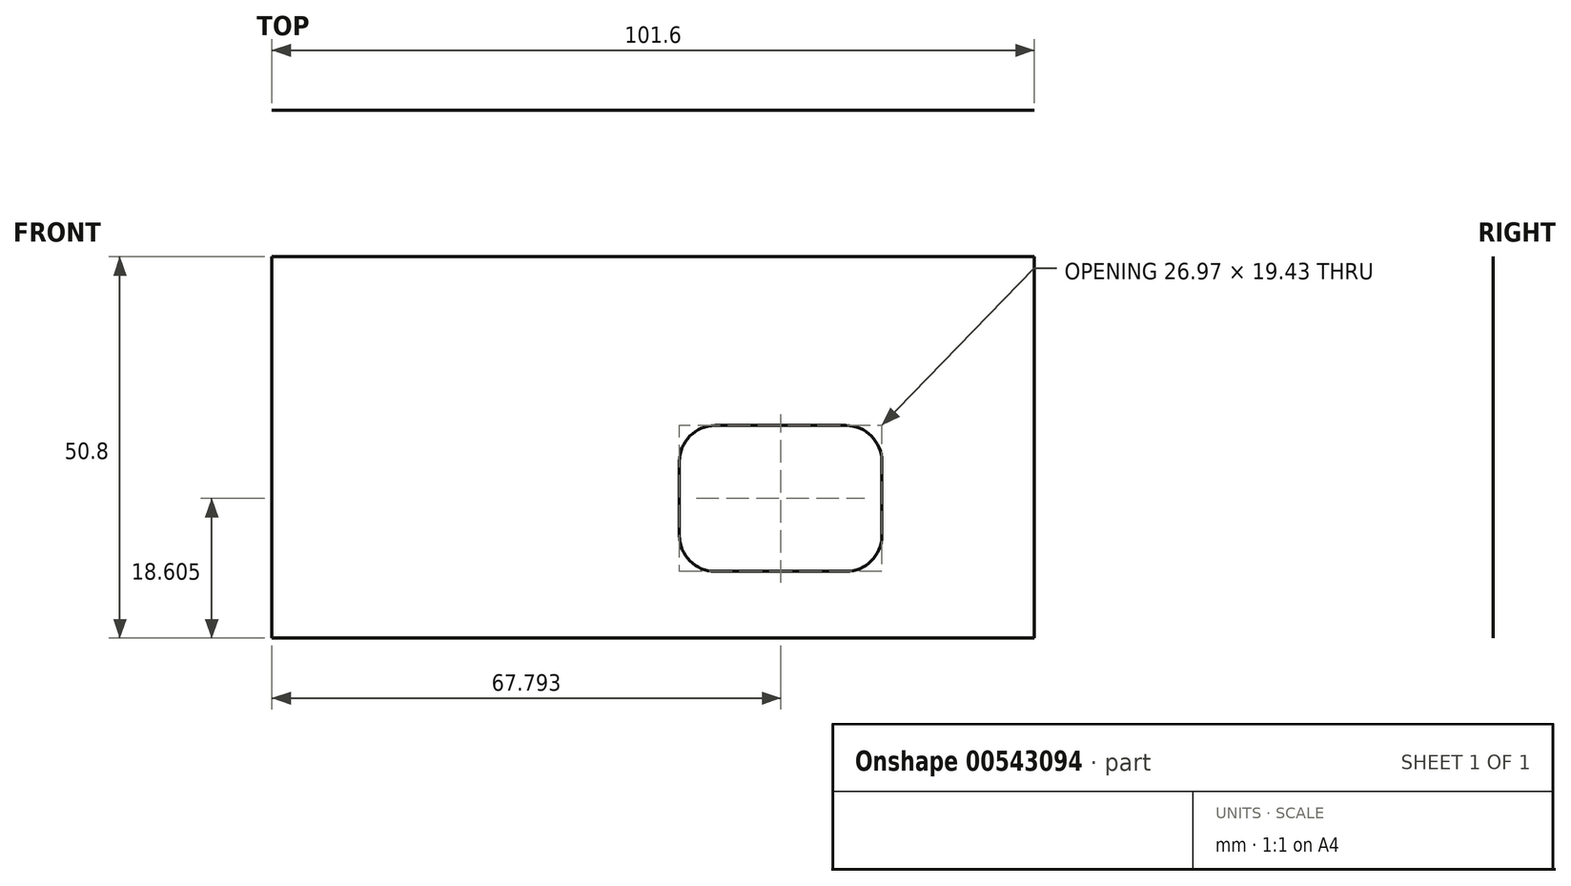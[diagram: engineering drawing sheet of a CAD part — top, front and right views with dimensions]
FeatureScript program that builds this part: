
annotation { "Feature Type Name" : "Feature", "Feature Type Description" : "" }
export const myFeature = defineFeature(function(context is Context, id is Id, definition is map)
    precondition{}
    {
        {
            var Q0;
            Q0=qCreatedBy(makeId("Front.planeOp"),FACE);
            var sketch = newSketch(context, id + "F0", { "sketchPlane" : qUnion([Q0])});
            skLineSegment(sketch, "E0.bottom", {"start": v(0, 0) * mm, "end": v(101.6, 0) * mm});
            skLineSegment(sketch, "E0.top", {"start": v(0, 50.8) * mm, "end": v(101.6, 50.8) * mm});
            skLineSegment(sketch, "E0.left", {"start": v(0, 0) * mm, "end": v(0, 50.8) * mm});
            skLineSegment(sketch, "E0.right", {"start": v(101.6, 0) * mm, "end": v(101.6, 50.8) * mm});
            skLineSegment(sketch, "E1.bottom", {"start": v(76.52, 8.9) * mm, "end": v(59.07, 8.89) * mm});
            skLineSegment(sketch, "E1.top", {"start": v(76.52, 28.32) * mm, "end": v(59.07, 28.32) * mm});
            skLineSegment(sketch, "E1.left", {"start": v(81.28, 13.65) * mm, "end": v(81.28, 23.56) * mm});
            skLineSegment(sketch, "E1.right", {"start": v(54.3, 13.65) * mm, "end": v(54.3, 23.56) * mm});
            skPoint(sketch, "E2.visualSharp", {"position": v(54.3, 28.32) * mm});
            skArc(sketch, "E2.filletArc", {"start": v(59.07, 28.32) * mm, "mid": v(55.7, 26.93) * mm, "end": v(54.3, 23.56) * mm});
            skPoint(sketch, "E3.visualSharp", {"position": v(54.3, 8.89) * mm});
            skArc(sketch, "E3.filletArc", {"start": v(54.3, 13.65) * mm, "mid": v(55.7, 10.28) * mm, "end": v(59.07, 8.89) * mm});
            skPoint(sketch, "E4.visualSharp", {"position": v(81.28, 28.32) * mm});
            skArc(sketch, "E4.filletArc", {"start": v(81.28, 23.56) * mm, "mid": v(79.89, 26.93) * mm, "end": v(76.52, 28.32) * mm});
            skPoint(sketch, "E5.visualSharp", {"position": v(81.28, 8.9) * mm});
            skArc(sketch, "E5.filletArc", {"start": v(76.52, 8.9) * mm, "mid": v(79.89, 10.28) * mm, "end": v(81.28, 13.65) * mm});
            skSolve(sketch);
        }
        {
            var Q0;
            Q0=makeQuery(id+"F0.imprint","IMPRINT",FACE,{"disambiguationData":[TD([[makeQuery(id+"F0.imprint","IMPRINT",EDGE,{"derivedFrom":sQuery(id+"F0.wireOp",EDGE,"E0.bottom")}),1.0]])]});
            extrude(context, id + "F1", {"entities" : qUnion([Q0]), "depth" : 1 / 406.4 * mm, "offsetDistance" : 25.4 * mm});
        }
    });
